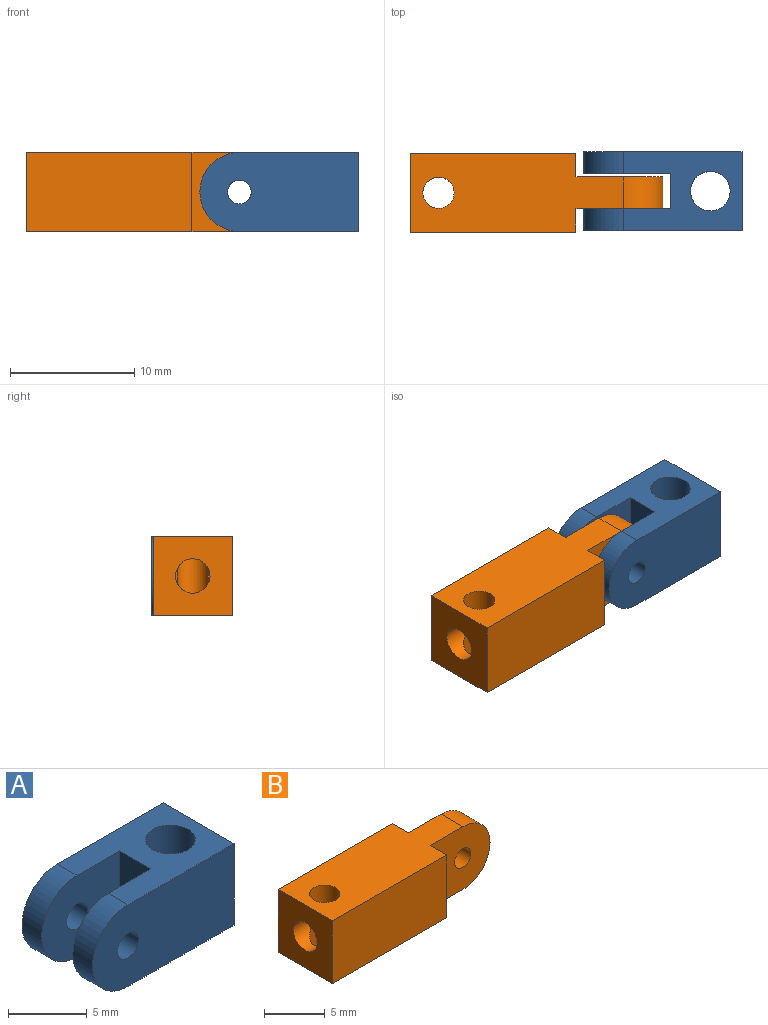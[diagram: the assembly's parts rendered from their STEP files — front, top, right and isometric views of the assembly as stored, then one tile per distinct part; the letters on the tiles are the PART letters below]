
ASSEMBLY  parts=2 mates=1
PART A: 13 faces, bbox 12.7x6.4x6.4 mm
  f0: plane 12.7x6.35mm, normal (0,1,0), area 73.5mm2, adj f4,f5,f6,f7,f12
  f1: plane 12.7x6.35mm, normal (0,-1,0), area 73.5mm2, adj f4,f5,f7,f8,f11
  f2: plane 6.99x6.35mm, normal (0,-1,0), area 37.2mm2, adj f4,f5,f6,f9,f12
  f3: plane 6.99x6.35mm, normal (0,1,0), area 37.2mm2, adj f4,f5,f8,f9,f11
  f4: plane 9.53x6.35mm, normal (0,0,1), area 41.9mm2, adj f0,f1,f2,f3,f7,f9,f10,f11
  f5: plane 9.53x6.35mm, normal (0,0,-1), area 41.9mm2, adj f0,f1,f2,f3,f7,f9,f10,f11
  f6: cylinder r=0.95mm len=1.91mm, axis (0,-1,0), area 10.6mm2, adj f0,f2
  f7: plane 6.35x6.35mm, normal (1,0,0), area 40.3mm2, adj f0,f1,f4,f5
  f8: cylinder r=0.95mm len=1.91mm, axis (0,-1,0), area 10.6mm2, adj f1,f3
  f9: plane 6.35x2.79mm, normal (-1,0,0), area 17.7mm2, adj f2,f3,f4,f5
  f10: cylinder r=1.59mm len=6.35mm, axis (0,0,1), area 63.3mm2, adj f4,f5
  f11: cylinder r=3.17mm len=6.35mm, axis (0,-1,0), area 17.7mm2, adj f1,f3,f4,f5
  f12: cylinder r=3.17mm len=6.35mm, axis (0,-1,0), area 17.7mm2, adj f0,f2,f4,f5
PART B: 15 faces, bbox 20.3x6.4x6.4 mm
  f0: plane 6.99x6.35mm, normal (0,-1,0), area 37.2mm2, adj f2,f3,f8,f10,f14
  f1: plane 6.99x6.35mm, normal (0,1,0), area 37.2mm2, adj f2,f3,f9,f10,f14
  f2: plane 17.15x6.35mm, normal (0,0,-1), area 89.4mm2, adj f0,f1,f4,f5,f6,f7,f8,f9
  f3: plane 17.15x6.35mm, normal (0,0,1), area 89.4mm2, adj f0,f1,f4,f5,f6,f7,f8,f9
  f4: cylinder r=1.26mm len=6.35mm, axis (0,0,1), area 42.1mm2, adj f2,f3,f11,f12,f13
  f5: plane 13.34x6.35mm, normal (0,1,0), area 84.7mm2, adj f2,f3,f7,f9
  f6: plane 13.34x6.35mm, normal (0,-1,0), area 84.7mm2, adj f2,f3,f7,f8
  f7: plane 6.35x6.35mm, normal (-1,0,0), area 34.3mm2, adj f2,f3,f5,f6,f11
  f8: plane 6.35x1.91mm, normal (1,0,0), area 12.1mm2, adj f0,f2,f3,f6
  f9: plane 6.35x1.91mm, normal (1,0,0), area 12.1mm2, adj f1,f2,f3,f5
  f10: cylinder r=0.95mm len=2.54mm, axis (0,-1,0), area 15.2mm2, adj f0,f1
  f11: cylinder r=1.38mm len=2.77mm, axis (-1,0,0), area 14.1mm2, adj f4,f7,f12,f13
  f12: plane 1.16x0.13mm, normal (-1,0,0), area 0.1mm2, adj f4,f11
  f13: plane 1.16x0.13mm, normal (-1,0,0), area 0.1mm2, adj f4,f11
  f14: cylinder r=3.17mm len=6.35mm, axis (0,-1,0), area 25.3mm2, adj f0,f1,f2,f3
PLACE A t=(28.17,2.89,2.53)mm
PLACE B t=(14.2,2.77,2.53)mm
MATE revolute A.f6 <-> B.f10  axis (0,1,0) through (31.34,4.67,5.71)mm
